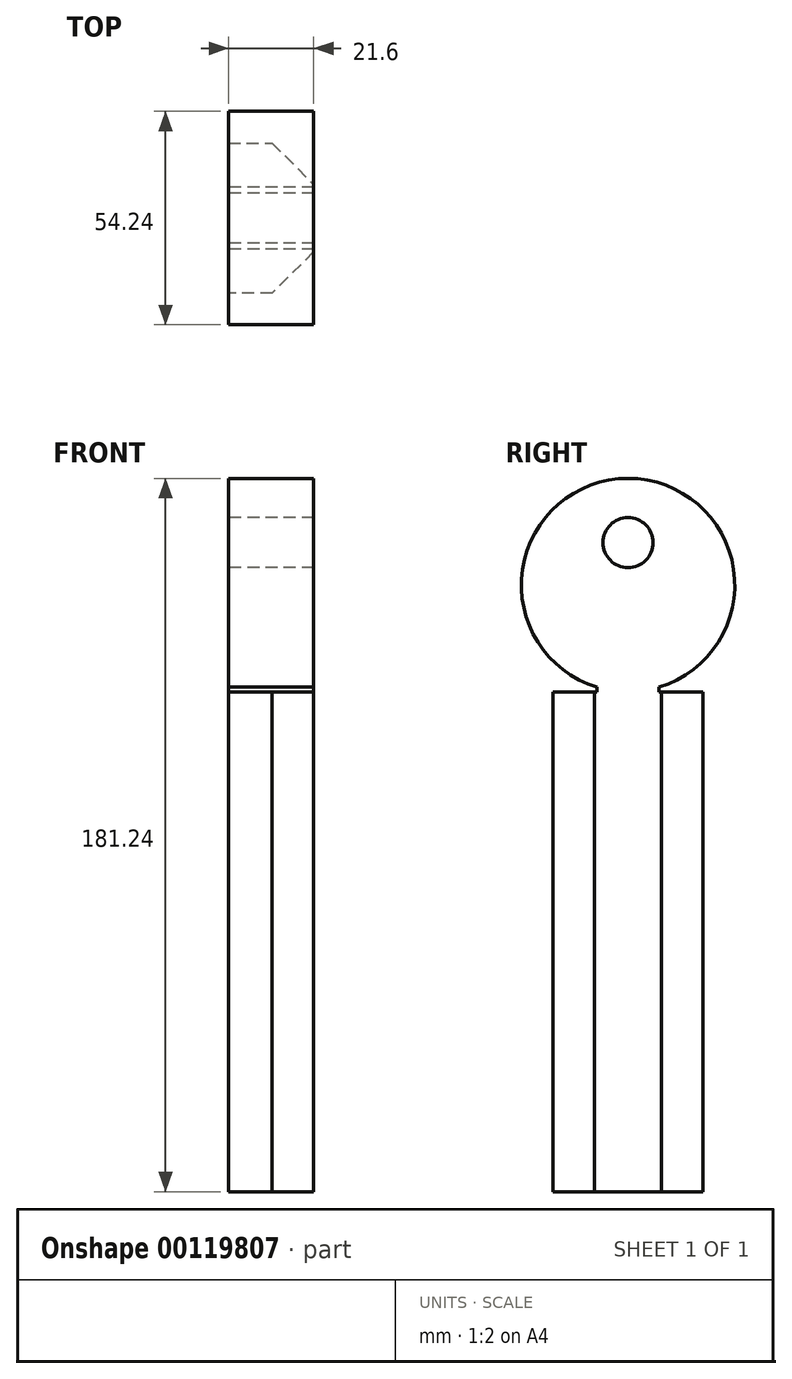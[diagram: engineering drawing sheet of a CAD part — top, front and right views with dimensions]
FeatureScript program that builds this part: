
annotation { "Feature Type Name" : "Feature", "Feature Type Description" : "" }
export const myFeature = defineFeature(function(context is Context, id is Id, definition is map)
    precondition{}
    {
        {
            var Q0;
            Q0=qCreatedBy(makeId("Top.planeOp"),FACE);
            var sketch = newSketch(context, id + "F0", { "sketchPlane" : qUnion([Q0])});
            skCircle(sketch, "E0.cCircle", {"center": v(-34.61, 21.32) * mm, "radius": 19.05 * mm, "construction": true});
            skLineSegment(sketch, "E0.0", {"start": v(-26.72, 2.27) * mm, "end": v(-42.5, 2.27) * mm});
            skLineSegment(sketch, "E0.1", {"start": v(-42.5, 2.27) * mm, "end": v(-53.66, 13.43) * mm});
            skLineSegment(sketch, "E0.2", {"start": v(-53.66, 13.43) * mm, "end": v(-53.66, 29.21) * mm});
            skLineSegment(sketch, "E0.3", {"start": v(-53.66, 29.21) * mm, "end": v(-42.5, 40.37) * mm});
            skLineSegment(sketch, "E0.4", {"start": v(-42.5, 40.37) * mm, "end": v(-26.72, 40.37) * mm});
            skLineSegment(sketch, "E0.5", {"start": v(-26.72, 40.37) * mm, "end": v(-15.56, 29.21) * mm});
            skLineSegment(sketch, "E0.6", {"start": v(-15.56, 29.21) * mm, "end": v(-15.56, 13.43) * mm});
            skLineSegment(sketch, "E0.7", {"start": v(-15.56, 13.43) * mm, "end": v(-26.72, 2.27) * mm});
            skPoint(sketch, "E0.0.midPoint", {"position": v(-34.61, 2.27) * mm});
            skSolve(sketch);
        }
        {
            var Q0;
            Q0 = qSketchRegion(id + "F0", true);
            extrude(context, id + "F1", {"entities" : qUnion([Q0]), "depth" : 127 * mm});
        }
        {
            var Q0;
            Q0=makeQuery(id+"F1.opExtrude","SWEPT_FACE",FACE,{"disambiguationData":[OSD([sQuery(id+"F0.wireOp",EDGE,"E0.6")])]});
            var sketch = newSketch(context, id + "F2", { "sketchPlane" : qUnion([Q0])});
            skCircle(sketch, "E1", {"center": v(21.32, 154.12) * mm, "radius": 27.12 * mm});
            skLineSegment(sketch, "E2.bottom", {"start": v(13.43, 122.32) * mm, "end": v(29.21, 122.32) * mm});
            skLineSegment(sketch, "E2.top", {"start": v(13.43, 154.12) * mm, "end": v(29.21, 154.12) * mm});
            skLineSegment(sketch, "E2.left", {"start": v(13.43, 122.32) * mm, "end": v(13.43, 154.12) * mm});
            skLineSegment(sketch, "E2.right", {"start": v(29.21, 122.32) * mm, "end": v(29.21, 154.12) * mm});
            skLineSegment(sketch, "E3", {"start": v(13.43, 154.12) * mm, "end": v(21.32, 154.12) * mm});
            skLineSegment(sketch, "E4", {"start": v(29.21, 154.12) * mm, "end": v(21.32, 154.12) * mm});
            skSolve(sketch);
        }
        {
            var Q0;
            Q0 = qSketchRegion(id + "F2", true);
            extrude(context, id + "F3", {"entities" : qUnion([Q0]), "operationType" : NewBodyOperationType.ADD, "oppositeDirection" : true, "depth" : 38.1 * mm});
        }
        {
            var Q0;
            Q0=makeQuery(id+"F3.boolean.opBoolean","MERGE",FACE,{"derivedFrom":[makeQuery(id+"F1.opExtrude","SWEPT_FACE",FACE,{"disambiguationData":[OSD([sQuery(id+"F0.wireOp",EDGE,"E0.2")])]}),makeQuery(id+"F3.opExtrude","CAP_FACE",FACE,{"disambiguationData":[OSD([sQuery(id+"F2.wireOp",EDGE,"E1"),sQuery(id+"F2.wireOp",EDGE,"E2.bottom"),sQuery(id+"F2.wireOp",EDGE,"E2.left"),sQuery(id+"F2.wireOp",EDGE,"E2.right")])],"isStart":false})]});
            var sketch = newSketch(context, id + "F4", { "sketchPlane" : qUnion([Q0])});
            skCircle(sketch, "E5", {"center": v(-21.32, 164.91) * mm, "radius": 6.35 * mm});
            skLineSegment(sketch, "E6", {"start": v(-29.21, 127) * mm, "end": v(-21.32, 164.91) * mm});
            skLineSegment(sketch, "E7", {"start": v(-21.32, 164.91) * mm, "end": v(-29.21, 0) * mm});
            skLineSegment(sketch, "E8", {"start": v(-29.21, 0) * mm, "end": v(-21.32, 164.91) * mm});
            skLineSegment(sketch, "E9", {"start": v(-13.43, 0) * mm, "end": v(-21.32, 164.91) * mm});
            skLineSegment(sketch, "E10", {"start": v(-21.32, 164.91) * mm, "end": v(-13.43, 127) * mm});
            skSolve(sketch);
        }
        {
            var Q0;
            {var subQ0=sQuery(id+"F4.wireOp",EDGE,"E6");var subQ1=sQuery(id+"F4.wireOp",EDGE,"E5");var subQ2=makeQuery(id+"F4.imprint","INTERSECT",VERTEX,{"derivedFrom":[subQ1,subQ0]});Q0=makeQuery(id+"F4.imprint","IMPRINT",FACE,{"disambiguationData":[TD([[makeQuery(id+"F4.imprint","IMPRINT",EDGE,{"disambiguationData":[TD([[subQ2,1.0]])],"derivedFrom":subQ1}),1.0]])]});}
            var Q1;
            {var subQ0=sQuery(id+"F4.wireOp",EDGE,"E8");var subQ1=sQuery(id+"F4.wireOp",EDGE,"E5");var subQ2=makeQuery(id+"F4.imprint","INTERSECT",VERTEX,{"derivedFrom":[subQ1,subQ0]});Q1=makeQuery(id+"F4.imprint","IMPRINT",FACE,{"disambiguationData":[TD([[makeQuery(id+"F4.imprint","IMPRINT",EDGE,{"disambiguationData":[TD([[subQ2,1.0]])],"derivedFrom":subQ1}),1.0]])]});}
            var Q2;
            {var subQ0=sQuery(id+"F4.wireOp",EDGE,"E8");var subQ1=sQuery(id+"F4.wireOp",EDGE,"E5");var subQ2=makeQuery(id+"F4.imprint","INTERSECT",VERTEX,{"derivedFrom":[subQ1,subQ0]});Q2=makeQuery(id+"F4.imprint","IMPRINT",FACE,{"disambiguationData":[TD([[makeQuery(id+"F4.imprint","IMPRINT",EDGE,{"disambiguationData":[TD([[subQ2,-1.0]])],"derivedFrom":subQ1}),1.0]])]});}
            var Q3;
            {var subQ0=sQuery(id+"F4.wireOp",EDGE,"E9");var subQ1=sQuery(id+"F4.wireOp",EDGE,"E5");var subQ2=makeQuery(id+"F4.imprint","INTERSECT",VERTEX,{"derivedFrom":[subQ1,subQ0]});Q3=makeQuery(id+"F4.imprint","IMPRINT",FACE,{"disambiguationData":[TD([[makeQuery(id+"F4.imprint","IMPRINT",EDGE,{"disambiguationData":[TD([[subQ2,-1.0]])],"derivedFrom":subQ1}),1.0]])]});}
            extrude(context, id + "F5", {"entities" : qUnion([Q0, Q1, Q2, Q3]), "operationType" : NewBodyOperationType.REMOVE, "endBound" : BoundingType.THROUGH_ALL, "oppositeDirection" : true, "depth" : 25.4 * mm});
        }
        {
            var Q0;
            Q0=makeQuery(id+"F3.boolean.opBoolean","MERGE",FACE,{"derivedFrom":[makeQuery(id+"F1.opExtrude","SWEPT_FACE",FACE,{"disambiguationData":[OSD([sQuery(id+"F0.wireOp",EDGE,"E0.6")])]}),makeQuery(id+"F3.opExtrude","CAP_FACE",FACE,{"disambiguationData":[OSD([sQuery(id+"F2.wireOp",EDGE,"E1"),sQuery(id+"F2.wireOp",EDGE,"E2.bottom"),sQuery(id+"F2.wireOp",EDGE,"E2.left"),sQuery(id+"F2.wireOp",EDGE,"E2.right")])],"isStart":true})]});
            var sketch = newSketch(context, id + "F6", { "sketchPlane" : qUnion([Q0])});
            skCircle(sketch, "E11", {"center": v(21.32, 154.12) * mm, "radius": 27.12 * mm});
            skLineSegment(sketch, "E12.bottom", {"start": v(-94.68, 0) * mm, "end": v(106.51, 0) * mm});
            skLineSegment(sketch, "E12.top", {"start": v(-94.68, 128.97) * mm, "end": v(106.51, 128.97) * mm});
            skLineSegment(sketch, "E12.left", {"start": v(-94.68, 0) * mm, "end": v(-94.68, 128.97) * mm});
            skLineSegment(sketch, "E12.right", {"start": v(106.51, 0) * mm, "end": v(106.51, 128.97) * mm});
            skSolve(sketch);
        }
        {
            var Q0;
            Q0 = qSketchRegion(id + "F6", true);
            var Q1;
            {var subQ0=sQuery(id+"F0.wireOp",EDGE,"E0.6");Q1=makeQuery(id+"F6.imprint","IMPRINT",FACE,{"disambiguationData":[TD([[makeQuery(id+"F6.imprint","IMPRINT",EDGE,{"derivedFrom":makeQuery(id+"F1.opExtrude","CAP_EDGE",EDGE,{"disambiguationData":[OSD([subQ0])],"isStart":true})}),-1.0]])]});}
            extrude(context, id + "F7", {"entities" : qUnion([Q0, Q1]), "operationType" : NewBodyOperationType.REMOVE, "oppositeDirection" : true, "depth" : ((1.5 / 2) - (0.25 / 2)) * mm});
        }
        {
            var Q0;
            Q0=makeQuery(id+"F3.boolean.opBoolean","MERGE",FACE,{"derivedFrom":[makeQuery(id+"F1.opExtrude","SWEPT_FACE",FACE,{"disambiguationData":[OSD([sQuery(id+"F0.wireOp",EDGE,"E0.2")])]}),makeQuery(id+"F3.opExtrude","CAP_FACE",FACE,{"disambiguationData":[OSD([sQuery(id+"F2.wireOp",EDGE,"E1"),sQuery(id+"F2.wireOp",EDGE,"E2.bottom"),sQuery(id+"F2.wireOp",EDGE,"E2.left"),sQuery(id+"F2.wireOp",EDGE,"E2.right")])],"isStart":false})]});
            var sketch = newSketch(context, id + "F8", { "sketchPlane" : qUnion([Q0])});
            skCircle(sketch, "E13", {"center": v(-21.32, 154.12) * mm, "radius": 27.12 * mm});
            skLineSegment(sketch, "E14.bottom", {"start": v(-111.61, 9.33) * mm, "end": v(141.51, 9.33) * mm});
            skLineSegment(sketch, "E14.top", {"start": v(-111.61, 263.33) * mm, "end": v(141.51, 263.33) * mm});
            skLineSegment(sketch, "E14.left", {"start": v(-111.61, 9.33) * mm, "end": v(-111.61, 263.33) * mm});
            skLineSegment(sketch, "E14.right", {"start": v(141.51, 9.33) * mm, "end": v(141.51, 263.33) * mm});
            skLineSegment(sketch, "E15.bottom", {"start": v(-93.46, -29.14) * mm, "end": v(147.98, -29.14) * mm});
            skLineSegment(sketch, "E15.top", {"start": v(-93.46, 39.5) * mm, "end": v(147.98, 39.5) * mm});
            skLineSegment(sketch, "E15.left", {"start": v(-93.46, -29.14) * mm, "end": v(-93.46, 39.5) * mm});
            skLineSegment(sketch, "E15.right", {"start": v(147.98, -29.14) * mm, "end": v(147.98, 39.5) * mm});
            skSolve(sketch);
        }
        {
            var Q0;
            {var subQ0=sQuery(id+"F8.wireOp",EDGE,"E13");Q0=makeQuery(id+"F8.imprint","IMPRINT",FACE,{"disambiguationData":[TD([[makeQuery(id+"F8.imprint","IMPRINT",EDGE,{"disambiguationData":[OD(0.0)],"derivedFrom":subQ0}),1.0]])]});}
            var Q1;
            Q1=makeQuery(id+"F8.imprint","IMPRINT",FACE,{"disambiguationData":[TD([[makeQuery(id+"F8.imprint","IMPRINT",EDGE,{"disambiguationData":[OD(1.0)],"derivedFrom":sQuery(id+"F8.wireOp",EDGE,"E13")}),1.0]])]});
            var Q2;
            {var subQ0=sQuery(id+"F8.wireOp",EDGE,"E14.right");var subQ1=sQuery(id+"F8.wireOp",EDGE,"E14.bottom");var subQ2=makeQuery(id+"F8.imprint","INTERSECT",VERTEX,{"derivedFrom":[subQ1,subQ0]});Q2=makeQuery(id+"F8.imprint","IMPRINT",FACE,{"disambiguationData":[TD([[makeQuery(id+"F8.imprint","IMPRINT",EDGE,{"disambiguationData":[TD([[subQ2,-1.0]])],"derivedFrom":subQ0}),1.0]])]});}
            var Q3;
            {var subQ0=sQuery(id+"F8.wireOp",EDGE,"E15.left");var subQ5=sQuery(id+"F8.wireOp",EDGE,"E15.top");var subQ6=makeQuery(id+"F8.imprint","INTERSECT",VERTEX,{"derivedFrom":[subQ5,subQ0]});Q3=makeQuery(id+"F8.imprint","IMPRINT",FACE,{"disambiguationData":[TD([[makeQuery(id+"F8.imprint","IMPRINT",EDGE,{"disambiguationData":[TD([[subQ6,1.0]])],"derivedFrom":subQ0}),-1.0]])]});}
            var Q4;
            {var subQ9=sQuery(id+"F8.wireOp",EDGE,"E15.bottom");Q4=makeQuery(id+"F8.imprint","IMPRINT",FACE,{"disambiguationData":[TD([[makeQuery(id+"F8.imprint","IMPRINT",EDGE,{"derivedFrom":subQ9}),1.0]])]});}
            var Q5;
            {var subQ0=sQuery(id+"F8.wireOp",EDGE,"E14.bottom");var subQ1=sQuery(id+"F0.wireOp",EDGE,"E0.2");var subQ2=makeQuery(id+"F1.opExtrude","SWEPT_EDGE",EDGE,{"disambiguationData":[OSD([subQ1,sQuery(id+"F0.wireOp",EDGE,"E0.3")])]});var subQ3=makeQuery(id+"F8.imprint","INTERSECT",VERTEX,{"derivedFrom":[subQ2,subQ0]});Q5=makeQuery(id+"F8.imprint","IMPRINT",FACE,{"disambiguationData":[TD([[makeQuery(id+"F8.imprint","IMPRINT",EDGE,{"disambiguationData":[TD([[subQ3,-1.0]])],"derivedFrom":subQ0}),1.0]])]});}
            var Q6;
            {var subQ1=sQuery(id+"F0.wireOp",EDGE,"E0.2");var subQ6=makeQuery(id+"F1.opExtrude","CAP_EDGE",EDGE,{"disambiguationData":[OSD([subQ1])],"isStart":true});Q6=makeQuery(id+"F8.imprint","IMPRINT",FACE,{"disambiguationData":[TD([[makeQuery(id+"F8.imprint","IMPRINT",EDGE,{"derivedFrom":subQ6}),-1.0]])]});}
            var Q7;
            Q7=makeQuery(id+"F8.imprint","IMPRINT",FACE,{"disambiguationData":[TD([[makeQuery(id+"F8.imprint","IMPRINT",EDGE,{"disambiguationData":[OD(0.0)],"derivedFrom":sQuery(id+"F8.wireOp",EDGE,"E13")}),-1.0]])]});
            extrude(context, id + "F9", {"entities" : qUnion([Q0, Q1, Q2, Q3, Q4, Q5, Q6, Q7]), "operationType" : NewBodyOperationType.REMOVE, "oppositeDirection" : true, "depth" : 15.88 * mm});
        }
    });
